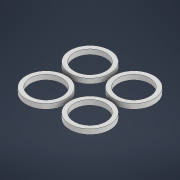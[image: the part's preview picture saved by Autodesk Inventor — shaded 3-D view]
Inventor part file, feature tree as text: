
AUTODESK INVENTOR PART (.ipt)
format: ipt  version: 2022 (Build 260153000, 153)  size: 115,712 bytes
history: native  units: mm
features: extrude x1, pattern_linear x1, sketch x1
ambient origin geometry x8: Origin, YZ Plane, XZ Plane, XY Plane, X Axis, Y Axis, Z Axis, Center Point
bodies: Solid1 (feature_tree)
feature tree (3):
  extrude  "Extrusion1"  Depth=9.0mm
  pattern_linear  "Rectangular Pattern1"  Spacing1=1.0mm  [1 undecoded]
  sketch  "Sketch1"  dims[d0=8.25mm d1=6.5mm d2=1.0mm d3=0.0mm d4=20.0mm d6=9.0mm d7=20.0mm d9=9.0mm]
note: 1 required parameter value undecoded (feature->parameter linkage not recoverable at this tier; creation-order binding heuristic only, values carry confidence <= 0.55)
